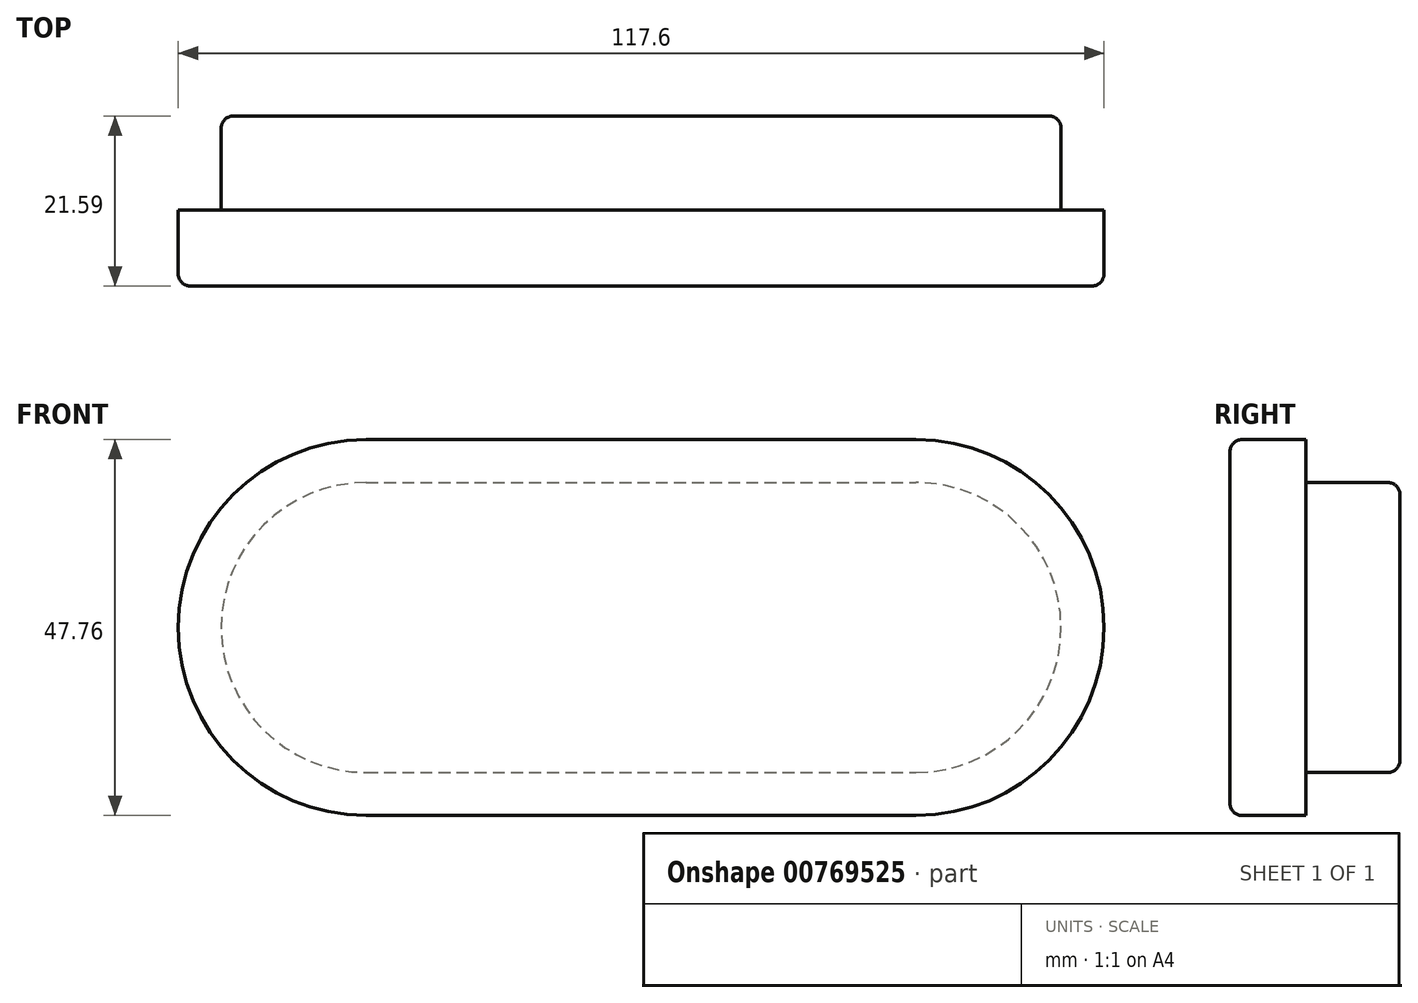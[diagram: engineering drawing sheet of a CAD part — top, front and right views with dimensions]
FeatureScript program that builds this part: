
annotation { "Feature Type Name" : "Feature", "Feature Type Description" : "" }
export const myFeature = defineFeature(function(context is Context, id is Id, definition is map)
    precondition{}
    {
        {
            var Q0;
            Q0=qCreatedBy(makeId("Front.planeOp"),FACE);
            var sketch = newSketch(context, id + "F0", { "sketchPlane" : qUnion([Q0])});
            skArc(sketch, "E0", {"start": v(-37.43, 18.41) * mm, "mid": v(-55.84, 0) * mm, "end": v(-37.43, -18.41) * mm});
            skArc(sketch, "E1", {"start": v(32.42, -18.41) * mm, "mid": v(50.84, 0) * mm, "end": v(32.42, 18.41) * mm});
            skLineSegment(sketch, "E2", {"start": v(-37.43, 18.41) * mm, "end": v(32.42, 18.41) * mm});
            skLineSegment(sketch, "E3", {"start": v(-37.43, -18.41) * mm, "end": v(32.42, -18.41) * mm});
            skSolve(sketch);
        }
        {
            var Q0;
            Q0 = qSketchRegion(id + "F0", true);
            extrude(context, id + "F1", {"entities" : qUnion([Q0]), "depth" : 11.94 * mm, "offsetDistance" : 25.4 * mm});
        }
        {
            var Q0;
            Q0=makeQuery(id+"F1.opExtrude","CAP_FACE",FACE,{"disambiguationData":[OSD([sQuery(id+"F0.wireOp",EDGE,"E0"),sQuery(id+"F0.wireOp",EDGE,"E1"),sQuery(id+"F0.wireOp",EDGE,"E2"),sQuery(id+"F0.wireOp",EDGE,"E3")])],"isStart":false});
            var sketch = newSketch(context, id + "F2", { "sketchPlane" : qUnion([Q0])});
            skArc(sketch, "E4", {"start": v(-37.43, 23.88) * mm, "mid": v(-61.3, 0) * mm, "end": v(-37.43, -23.88) * mm});
            skArc(sketch, "E5", {"start": v(32.42, -23.88) * mm, "mid": v(56.3, 0) * mm, "end": v(32.42, 23.88) * mm});
            skLineSegment(sketch, "E6", {"start": v(-37.43, 23.88) * mm, "end": v(32.42, 23.88) * mm});
            skLineSegment(sketch, "E7", {"start": v(-37.43, -23.88) * mm, "end": v(32.42, -23.88) * mm});
            skSolve(sketch);
        }
        {
            var Q0;
            Q0 = qSketchRegion(id + "F2", true);
            extrude(context, id + "F3", {"entities" : qUnion([Q0]), "operationType" : NewBodyOperationType.ADD, "depth" : 9.65 * mm, "offsetDistance" : 25.4 * mm});
        }
        {
            var Q0;
            Q0=makeQuery(id+"F3.opExtrude","CAP_FACE",FACE,{"disambiguationData":[OSD([sQuery(id+"F2.wireOp",EDGE,"E4"),sQuery(id+"F2.wireOp",EDGE,"E5"),sQuery(id+"F2.wireOp",EDGE,"E6"),sQuery(id+"F2.wireOp",EDGE,"E7")])],"isStart":false});
            var Q1;
            Q1=makeQuery(id+"F1.opExtrude","CAP_FACE",FACE,{"disambiguationData":[OSD([sQuery(id+"F0.wireOp",EDGE,"E0"),sQuery(id+"F0.wireOp",EDGE,"E1"),sQuery(id+"F0.wireOp",EDGE,"E2"),sQuery(id+"F0.wireOp",EDGE,"E3")])],"isStart":true});
            fillet(context, id + "F4", {"entities" : qUnion([Q0, Q1]), "radius" : 1.52 * mm, "tangentPropagation" : true, "allowEdgeOverflow" : false});
        }
    });
